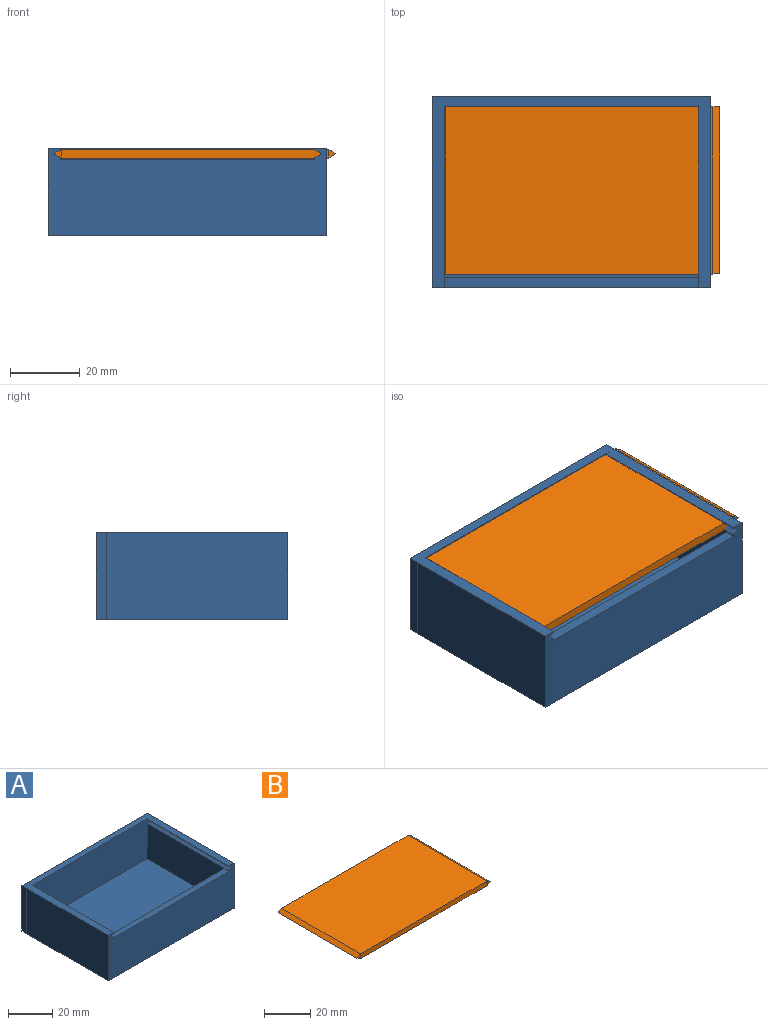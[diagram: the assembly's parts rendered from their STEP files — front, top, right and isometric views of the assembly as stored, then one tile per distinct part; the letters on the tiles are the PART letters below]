
ASSEMBLY  parts=2 mates=1
PART A: 20 faces, bbox 80x55x25 mm
  f0: plane 73.2x49mm, normal (0,0,1), area 3587mm2, adj f7,f14,f15,f19
  f1: plane 52x1.9mm, normal (0.5,0,0.87), area 114mm2, adj f2,f7,f8,f15
  f2: plane 52x1.9mm, normal (0.5,0,-0.87), area 114mm2, adj f1,f3,f8,f15
  f3: plane 52x0.4mm, normal (1,0,0), area 21mm2, adj f2,f4,f8,f15
  f4: plane 80.01x55mm, normal (0,0,1), area 593.4mm2, adj f3,f5,f8,f9,f12,f13,f15,f16
  f5: plane 52x25mm, normal (-1,0,0), area 1300mm2, adj f4,f6,f8,f16
  f6: plane 80.01x55mm, normal (0,0,-1), area 4400mm2, adj f5,f8,f9,f13,f16,f17
  f7: plane 52x19.43mm, normal (1,0,0), area 953.8mm2, adj f0,f1,f8,f15,f18,f19
  f8: plane 80x25mm, normal (0,-1,0), area 1770.1mm2, adj f1,f2,f3,f4,f5,f6,f7,f10
  f9: plane 80.01x25mm, normal (0,1,0), area 2000.4mm2, adj f4,f6,f13,f17
  f10: plane 52x1.9mm, normal (-0.5,0,0.87), area 114mm2, adj f8,f11,f14,f15
  f11: plane 52x1.9mm, normal (-0.5,0,-0.87), area 114mm2, adj f8,f10,f12,f15
  f12: plane 52x0.4mm, normal (-1,0,0), area 21mm2, adj f4,f8,f11,f15
  f13: plane 55x25mm, normal (1,0,0), area 1375mm2, adj f4,f6,f8,f9
  f14: plane 52x19.43mm, normal (-1,0,0), area 953.8mm2, adj f0,f8,f10,f15,f18,f19
  f15: plane 77x22.03mm, normal (0,-1,0), area 1616.9mm2, adj f0,f1,f2,f3,f4,f7,f10,f11
  f16: plane 25x0.01mm, normal (0,-1,0), area 0.4mm2, adj f4,f5,f6,f17
  f17: plane 25x3mm, normal (-1,0,0), area 75mm2, adj f4,f6,f9,f16
  f18: plane 73.2x3mm, normal (0,0,1), area 219.6mm2, adj f7,f8,f14,f19
  f19: plane 73.2x18.95mm, normal (0,1,0), area 1387mm2, adj f0,f7,f14,f18
PART B: 12 faces, bbox 81.1x48.1x2.5 mm
  f0: plane 2.5x0.11mm, normal (-1,0,0), area 0.3mm2, adj f2,f4,f5,f11
  f1: plane 2.5x0.11mm, normal (1,0,0), area 0.3mm2, adj f2,f4,f5,f8
  f2: plane 77x2.5mm, normal (0,-1,0), area 192.5mm2, adj f0,f1,f4,f5
  f3: plane 81.06x2.5mm, normal (0,1,0), area 197.6mm2, adj f4,f5,f6,f7,f9,f10
  f4: plane 77x48.11mm, normal (0,0,1), area 3704.2mm2, adj f0,f1,f2,f3,f6,f9
  f5: plane 77x48.11mm, normal (0,0,-1), area 3704.2mm2, adj f0,f1,f2,f3,f7,f10
  f6: plane 48x1.9mm, normal (0.55,0,0.84), area 109.1mm2, adj f3,f4,f7,f8
  f7: plane 48x1.9mm, normal (0.55,0,-0.84), area 109.1mm2, adj f3,f5,f6,f8
  f8: plane 2.5x1.9mm, normal (0,-1,0), area 2.4mm2, adj f1,f6,f7
  f9: plane 48x2.17mm, normal (-0.5,0,0.87), area 120mm2, adj f3,f4,f10,f11
  f10: plane 48x2.17mm, normal (-0.5,0,-0.87), area 120mm2, adj f3,f5,f9,f11
  f11: plane 2.5x2.17mm, normal (0,-1,0), area 2.7mm2, adj f0,f9,f10
PLACE A t=(14.16,-65.05,-59.32)mm fixed
PLACE B t=(13.41,-119.37,-37.07)mm
MATE slider A.f15 <-> B.f3  axis (0,-1,0) through (-24.34,-68.05,-35.82)mm
